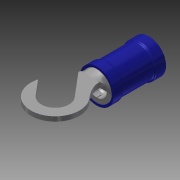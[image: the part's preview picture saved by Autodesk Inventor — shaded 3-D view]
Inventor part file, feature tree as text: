
AUTODESK INVENTOR PART (.ipt)
format: ipt  version: 2014 (Build 180170000, 170)  size: 523,264 bytes
history: native  units: in
note: dims shown in document units (in); Inventor stores cm internally (conversion verified against a paired STEP export)
features: sketch x7, fillet x6, projected_geometry x6, extrude x5, mirror x1, shell x1, revolve x1, plane x1, loft x1, chamfer x1, other x1
ambient origin geometry x8: Origin, YZ Plane, XZ Plane, XY Plane, X Axis, Y Axis, Z Axis, Center Point
bodies: Solid1 (feature_tree), Solid2 (feature_tree)
feature tree (31):
  extrude  "Extrusion1"  Depth=0.229in TaperAngle=0.0deg
  extrude  "Extrusion2"  Depth=0.068in TaperAngle=0.0deg
  fillet  "Fillet1"  Radius=0.01in
  mirror  "Mirror1"
  shell  "Shell1"  Thickness=0.0175in
  revolve  "Revolution1"  [1 undecoded]
  plane  "Work Plane1"
  extrude  "Extrusion3"  Depth=0.082in
  loft  "Loft1"
  fillet  "Fillet2"  Radius=0.339in
  fillet  "Fillet3"  Radius=0.073in
  fillet  "Fillet4"  Radius=0.032in
  fillet  "Fillet5"  [1 undecoded]
  chamfer  "Chamfer1"  Angle=90.0deg  [1 undecoded]
  extrude  "Extrusion4"  Depth=0.015in
  extrude  "Extrusion5"  Depth=0.02in
  fillet  "Fillet6"  Radius=0.003in
  sketch  "Sketch1"  dims[d0=0.219in d1=0.229in d2=0.0in]
  sketch  "Sketch2"  dims[d3=0.236in d4=0.068in d5=0.0in d6=0.01in d7=0.0175in]
  projected_geometry  "Projected Loop1"
  sketch  "Sketch3"  dims[d8=0.031in d9=0.031in]
  sketch  "Sketch4"  dims[d10=90.0deg d11=0.082in]
  projected_geometry  "Projected Loop2"
  sketch  "Sketch5"  dims[d12=0.2905in d13=0.0495in d14=0.339in d15=0.073in d16=0.032in d17=0.0in d18=0.0in d19=90.0deg d20=0.0in d21=90.0deg]
  projected_geometry  "Projected Loop3"
  other  "Edges1"
  sketch  "Sketch6"  dims[d22=0.1in d23=0.015in]
  sketch  "Sketch7"  dims[d24=0.02in d25=0.02in d26=0.003in d27=0.125in d28=45.0deg d29=0.005in d30=0.032in d31=0.0in d32=1.0in d33=0.0in d34=0.02in]
  projected_geometry  "Projected Loop4"
  projected_geometry  "Project Cut Edges1"
  projected_geometry  "Project Cut Edges2"
note: 3 required parameter values undecoded (feature->parameter linkage not recoverable at this tier; creation-order binding heuristic only, values carry confidence <= 0.55)